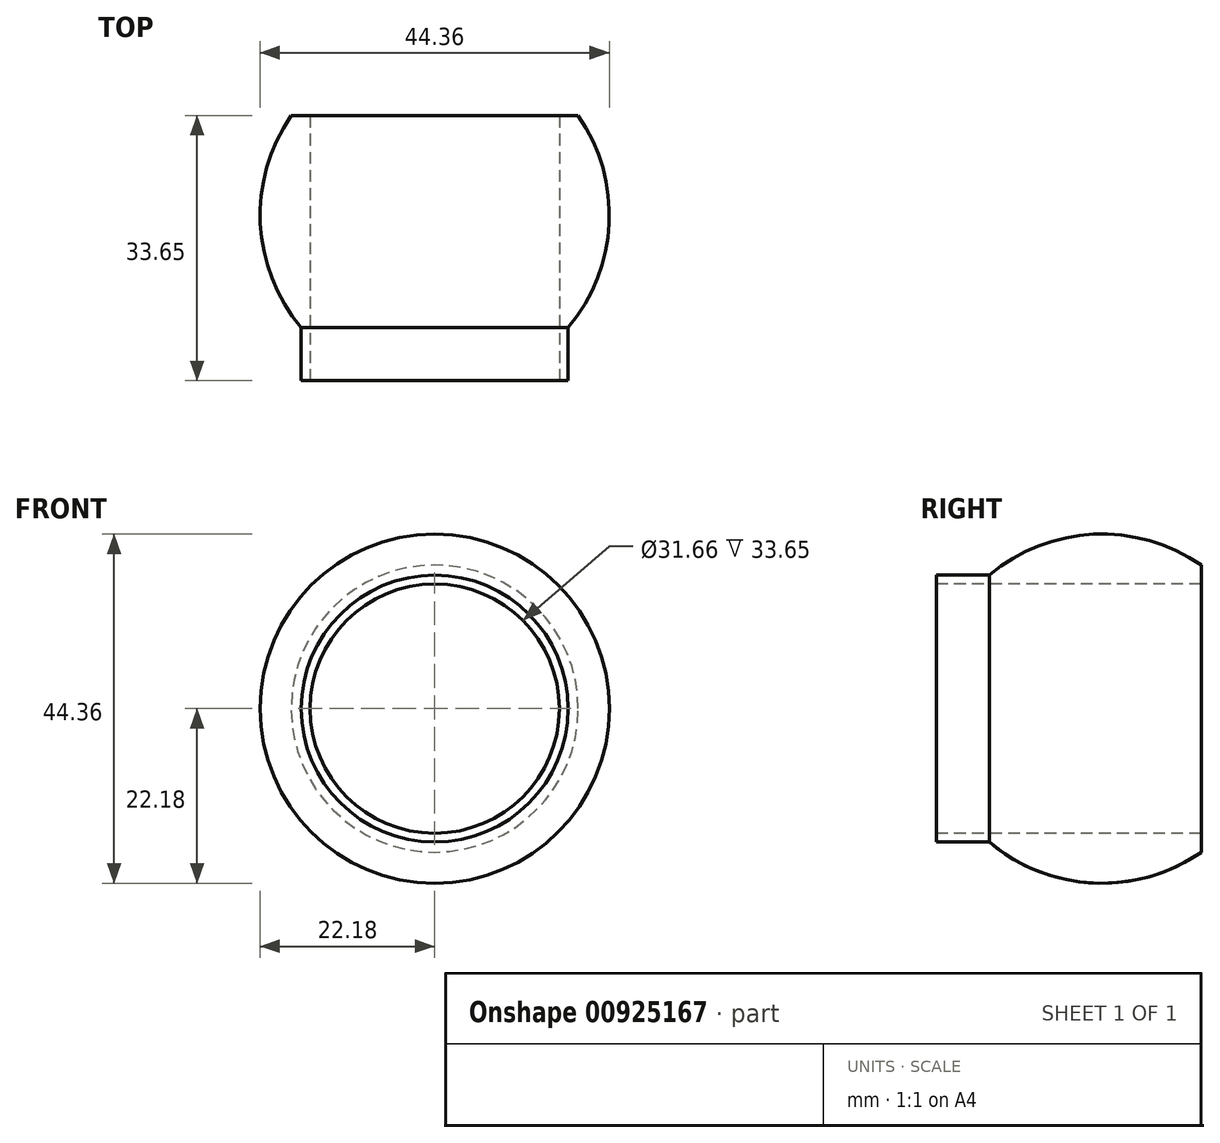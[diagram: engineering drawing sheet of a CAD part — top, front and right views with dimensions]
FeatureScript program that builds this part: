
annotation { "Feature Type Name" : "Feature", "Feature Type Description" : "" }
export const myFeature = defineFeature(function(context is Context, id is Id, definition is map)
    precondition{}
    {
        {
            var Q0;
            Q0=qCreatedBy(makeId("Right.planeOp"),FACE);
            var sketch = newSketch(context, id + "F0", { "sketchPlane" : qUnion([Q0])});
            skLineSegment(sketch, "E0", {"start": v(-31.67, 0) * mm, "end": v(38.06, 0) * mm, "construction": true});
            skArc(sketch, "E1", {"start": v(22.18, 0) * mm, "mid": v(0, 22.18) * mm, "end": v(-22.18, 0) * mm});
            skLineSegment(sketch, "E2", {"start": v(-22.18, 0) * mm, "end": v(22.18, 0) * mm});
            skSolve(sketch);
        }
        {
            var Q0;
            Q0 = qSketchRegion(id + "F0", true);
            var Q1;
            Q1=sQuery(id+"F0.wireOp",EDGE,"E0");
            revolve(context, id + "F1", {"surfaceOperationType" : NewSurfaceOperationType.NEW, "entities" : qUnion([Q0]), "axis" : qUnion([Q1]), "revolveType" : RevolveType.FULL});
        }
        {
            var Q0;
            Q0=qCreatedBy(makeId("Front.planeOp"),FACE);
            var sketch = newSketch(context, id + "F2", { "sketchPlane" : qUnion([Q0])});
            skCircle(sketch, "E3", {"center": v(0, 0) * mm, "radius": 16.95 * mm});
            skSolve(sketch);
        }
        {
            var Q0;
            Q0 = qSketchRegion(id + "F2", true);
            extrude(context, id + "F3", {"entities" : qUnion([Q0]), "operationType" : NewBodyOperationType.ADD, "depth" : 21.02 * mm, "offsetDistance" : 25 * mm});
        }
        {
            var Q0;
            Q0=makeQuery(id+"F3.opExtrude","CAP_FACE",FACE,{"disambiguationData":[OSD([sQuery(id+"F2.wireOp",EDGE,"E3")])],"isStart":false});
            var sketch = newSketch(context, id + "F4", { "sketchPlane" : qUnion([Q0])});
            skCircle(sketch, "E4", {"center": v(0, 0) * mm, "radius": 15.83 * mm});
            skSolve(sketch);
        }
        {
            var Q0;
            Q0 = qSketchRegion(id + "F4", true);
            extrude(context, id + "F5", {"entities" : qUnion([Q0]), "operationType" : NewBodyOperationType.REMOVE, "oppositeDirection" : true, "depth" : 100 * mm, "offsetDistance" : 25 * mm, "symmetric" : true});
        }
        {
            var Q0;
            Q0=qCreatedBy(makeId("Right.planeOp"),FACE);
            var sketch = newSketch(context, id + "F6", { "sketchPlane" : qUnion([Q0])});
            skLineSegment(sketch, "E5.bottom", {"start": v(20, 30) * mm, "end": v(12.63, 30) * mm});
            skLineSegment(sketch, "E5.top", {"start": v(20, -30) * mm, "end": v(12.63, -30) * mm});
            skLineSegment(sketch, "E5.left", {"start": v(20, 30) * mm, "end": v(20, -30) * mm});
            skLineSegment(sketch, "E5.right", {"start": v(12.63, 30) * mm, "end": v(12.63, -30) * mm});
            skSolve(sketch);
        }
        {
            var Q0;
            Q0 = qSketchRegion(id + "F6", true);
            extrude(context, id + "F7", {"entities" : qUnion([Q0]), "operationType" : NewBodyOperationType.REMOVE, "oppositeDirection" : true, "depth" : 100 * mm, "offsetDistance" : 25 * mm, "symmetric" : true});
        }
    });
